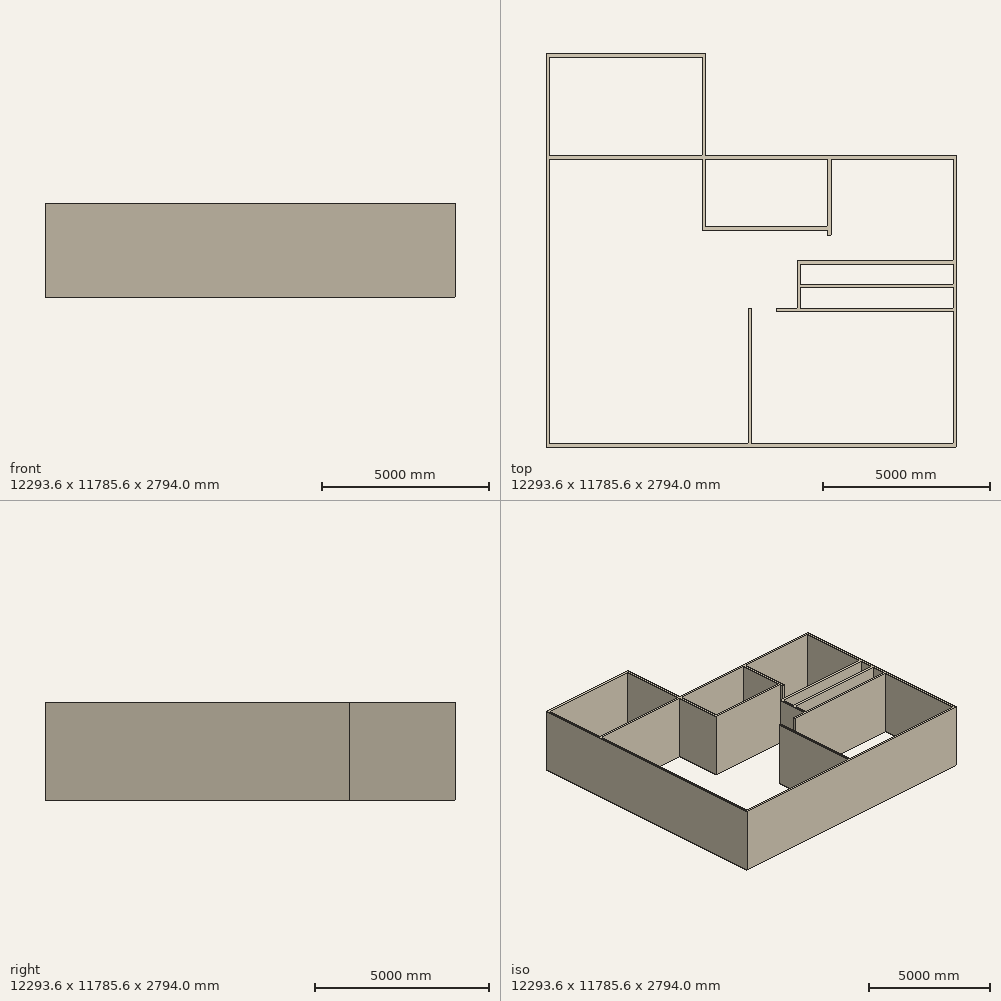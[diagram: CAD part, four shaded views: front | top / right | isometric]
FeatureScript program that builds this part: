
annotation { "Feature Type Name" : "Feature", "Feature Type Description" : "" }
export const myFeature = defineFeature(function(context is Context, id is Id, definition is map)
    precondition{}
    {
        {
            var Q0;
            Q0=qCreatedBy(makeId("Top.planeOp"),FACE);
            var sketch = newSketch(context, id + "F0", { "sketchPlane" : qUnion([Q0])});
            skLineSegment(sketch, "E0.bottom", {"start": v(0, 0) * mm, "end": v(-6045.2, 0) * mm});
            skLineSegment(sketch, "E0.top", {"start": v(0, 8534.4) * mm, "end": v(-3657.6, 8534.4) * mm});
            skLineSegment(sketch, "E0.left", {"start": v(0, 0) * mm, "end": v(0, 3962.4) * mm});
            skLineSegment(sketch, "E0.right", {"start": v(-12090.4, 0) * mm, "end": v(-12090.4, 8534.4) * mm});
            skLineSegment(sketch, "E1", {"start": v(-6146.8, 4064) * mm, "end": v(-6146.8, 0) * mm});
            skLineSegment(sketch, "E2", {"start": v(-5283.2, 3962.4) * mm, "end": v(0, 3962.4) * mm});
            skLineSegment(sketch, "E3", {"start": v(0, 5486.4) * mm, "end": v(-4673.6, 5486.4) * mm});
            skLineSegment(sketch, "E4", {"start": v(-4673.6, 5486.4) * mm, "end": v(-4673.6, 4064) * mm});
            skLineSegment(sketch, "E5", {"start": v(0, 4724.4) * mm, "end": v(-4572, 4724.4) * mm, "construction": true});
            skLineSegment(sketch, "E6", {"start": v(0, 4775.2) * mm, "end": v(-4572, 4775.2) * mm});
            skLineSegment(sketch, "E7", {"start": v(0, 4673.6) * mm, "end": v(-4572, 4673.6) * mm});
            skLineSegment(sketch, "E8.0", {"start": v(101.6, -101.6) * mm, "end": v(101.6, 8636) * mm});
            skLineSegment(sketch, "E8.1", {"start": v(101.6, -101.6) * mm, "end": v(-12192, -101.6) * mm});
            skLineSegment(sketch, "E8.2", {"start": v(-12192, -101.6) * mm, "end": v(-12192, 8636) * mm});
            skLineSegment(sketch, "E8.3", {"start": v(101.6, 8636) * mm, "end": v(-7416.8, 8636) * mm});
            skLineSegment(sketch, "E9.0", {"start": v(-5283.2, 4064) * mm, "end": v(-4673.6, 4064) * mm});
            skLineSegment(sketch, "E10.0", {"start": v(-4572, 5384.8) * mm, "end": v(-4572, 4775.2) * mm});
            skLineSegment(sketch, "E10.1", {"start": v(0, 5384.8) * mm, "end": v(-4572, 5384.8) * mm});
            skLineSegment(sketch, "E11", {"start": v(-5283.2, 4064) * mm, "end": v(-5283.2, 3962.4) * mm});
            skLineSegment(sketch, "E12.trimOffspring", {"start": v(-4572, 4673.6) * mm, "end": v(-4572, 4064) * mm});
            skLineSegment(sketch, "E13.trimOffspring", {"start": v(-4572, 4064) * mm, "end": v(0, 4064) * mm});
            skLineSegment(sketch, "E14.trimOffspring", {"start": v(0, 5486.4) * mm, "end": v(0, 8534.4) * mm});
            skLineSegment(sketch, "E15.trimOffspring", {"start": v(0, 4775.2) * mm, "end": v(0, 5384.8) * mm});
            skLineSegment(sketch, "E16.trimOffspring", {"start": v(0, 4064) * mm, "end": v(0, 4673.6) * mm});
            skLineSegment(sketch, "E17.0", {"start": v(-6045.2, 4064) * mm, "end": v(-6045.2, 0) * mm});
            skLineSegment(sketch, "E18", {"start": v(-6045.2, 4064) * mm, "end": v(-6146.8, 4064) * mm});
            skLineSegment(sketch, "E19.trimOffspring", {"start": v(-6146.8, 0) * mm, "end": v(-12090.4, 0) * mm});
            skLineSegment(sketch, "E20", {"start": v(-3657.6, 8534.4) * mm, "end": v(-3657.6, 6248.4) * mm});
            skLineSegment(sketch, "E21", {"start": v(-3759.2, 6502.4) * mm, "end": v(-3759.2, 8534.4) * mm});
            skLineSegment(sketch, "E22.trimOffspring", {"start": v(-3759.2, 8534.4) * mm, "end": v(-7416.8, 8534.4) * mm});
            skLineSegment(sketch, "E23", {"start": v(-7518.4, 6400.8) * mm, "end": v(-3759.2, 6400.8) * mm});
            skLineSegment(sketch, "E24.left", {"start": v(-7518.4, 8534.4) * mm, "end": v(-7518.4, 6400.8) * mm});
            skLineSegment(sketch, "E24.right", {"start": v(-7416.8, 8534.4) * mm, "end": v(-7416.8, 6502.4) * mm});
            skLineSegment(sketch, "E25.trimOffspring", {"start": v(-7518.4, 8534.4) * mm, "end": v(-12090.4, 8534.4) * mm});
            skLineSegment(sketch, "E26", {"start": v(-3759.2, 6502.4) * mm, "end": v(-7416.8, 6502.4) * mm});
            skLineSegment(sketch, "E27", {"start": v(-3657.6, 6248.4) * mm, "end": v(-3759.2, 6248.4) * mm});
            skLineSegment(sketch, "E28", {"start": v(-3759.2, 6248.4) * mm, "end": v(-3759.2, 6400.8) * mm});
            skLineSegment(sketch, "E29", {"start": v(-12192, 8636) * mm, "end": v(-12192, 11684) * mm});
            skLineSegment(sketch, "E30", {"start": v(-12192, 11684) * mm, "end": v(-7416.8, 11684) * mm});
            skLineSegment(sketch, "E31", {"start": v(-7416.8, 8636) * mm, "end": v(-7416.8, 11684) * mm});
            skLineSegment(sketch, "E32.0", {"start": v(-7518.4, 8636) * mm, "end": v(-7518.4, 11582.4) * mm});
            skLineSegment(sketch, "E32.1", {"start": v(-12090.4, 11582.4) * mm, "end": v(-7518.4, 11582.4) * mm});
            skLineSegment(sketch, "E32.2", {"start": v(-12090.4, 8636) * mm, "end": v(-12090.4, 11582.4) * mm});
            skLineSegment(sketch, "E33.trimOffspring", {"start": v(-7518.4, 8636) * mm, "end": v(-12090.4, 8636) * mm});
            skSolve(sketch);
        }
        {
            var Q0;
            Q0=makeQuery(id+"F0.imprint","IMPRINT",FACE,{"disambiguationData":[TD([[makeQuery(id+"F0.imprint","IMPRINT",EDGE,{"derivedFrom":sQuery(id+"F0.wireOp",EDGE,"E0.bottom")}),1.0]])]});
            extrude(context, id + "F1", {"entities" : qUnion([Q0]), "depth" : 2794 * mm});
        }
    });
